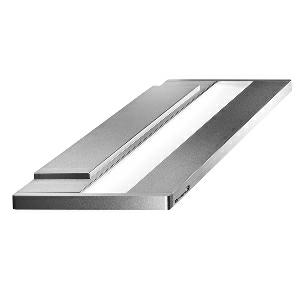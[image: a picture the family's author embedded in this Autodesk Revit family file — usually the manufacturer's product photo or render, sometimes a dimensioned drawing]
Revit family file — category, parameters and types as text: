
# Revit family: zera_bed_-_zew_7000_830_-_lvc_00813016_b575
name_source: partatom
category: Lighting Fixtures
units: mm (PartAtom-declared; Revit-internal decimal feet)

## family parameters
Cut with Voids When Loaded = No
Host = Face
Light Source = No
Part Type = Normal
Room Calculation Point = No
Round Connector Dimension = Use Diameter
Shared = No

## types (1)
- AL+LL (1 x LED, 6900 lm, 4000K/3000K)
    Apparent Load = 61 VA
    Approval mark = CE
    CIE Flux Codes = 49 80 96 25 100
    Color Rendering = 90/80
    Color Temperature = 4000K/3000K
    Default Elevation = 2000 mm  [stored 6.56168 ft]
    Description = ZEW 7000/830|Wall-mounted luminaire|light source:   Warm white   |work equipment: Power supply unit|luminous flux: 6900 lm|light distribution: Direct/indirect|class of protection: I|technology: Switchable|mains lead: Connector 5 pin|glare control: Diffusor|special features: General light, indirect, 3000K, Ra80, DIN EN 60598-2-25, Reading light, direct, 3,00K, Ra80, Protective low voltage relay (LVC)|
    Frequency = 50 Hz, 60 Hz
    Height = 20 mm  [stored 0.0656168 ft]
    Lamp = 1 x LED
    Lamp Light Flux = 6900 lm
    Lamp count = 1
    Length = 1050 mm
    Luminous efficacy = 113 lm/W
    Manufacturer = Waldmann
    ModVariant = No
    Model = 00813016
    Mounting Place = Wall
    Mounting Type = Surface mounted
    Number of Poles = 1
    OnlyDefault = Yes
    Power Factor = 1
    Product Name = ZERA.bed - ZEW 7000/830 - LVC
    Product group = Wall mounted Luminaire
    ProductGroupID = 20
    Protection Class = Protection class I
    Protection Degree = IP 20
    RLX_Detail_Level = 1
    RLX_Emergency_Light_Flux = 0 lm
    RLX_Emergency_Type = 0
    RLX_Emergency_Type_DB = No
    RlxData = <blob elided: 69917 chars, md5=1bb2d786>
    Socket = socket
    Standby Power = 0 W
    System Light Flux = 6900 lm
    System Power = 61 W
    Type Comments = Allgemeinlicht und Leselicht
    Type Image = zera_bed.jpg
    URL = http://relux.com
    VarID = al_ll_67c3
    Voltage = 230 V
    Voltage Range = 220-240 V
    Weight = 0.00 kg
    Width = 230 mm

note: [stored X ft] marks values corroborated as IEEE doubles in the binary element streams (Revit-internal decimal feet)

## geometry (parser evidence)
native form markers: Blend x4, Sweep x12
no freeform markers — native parametric forms only
